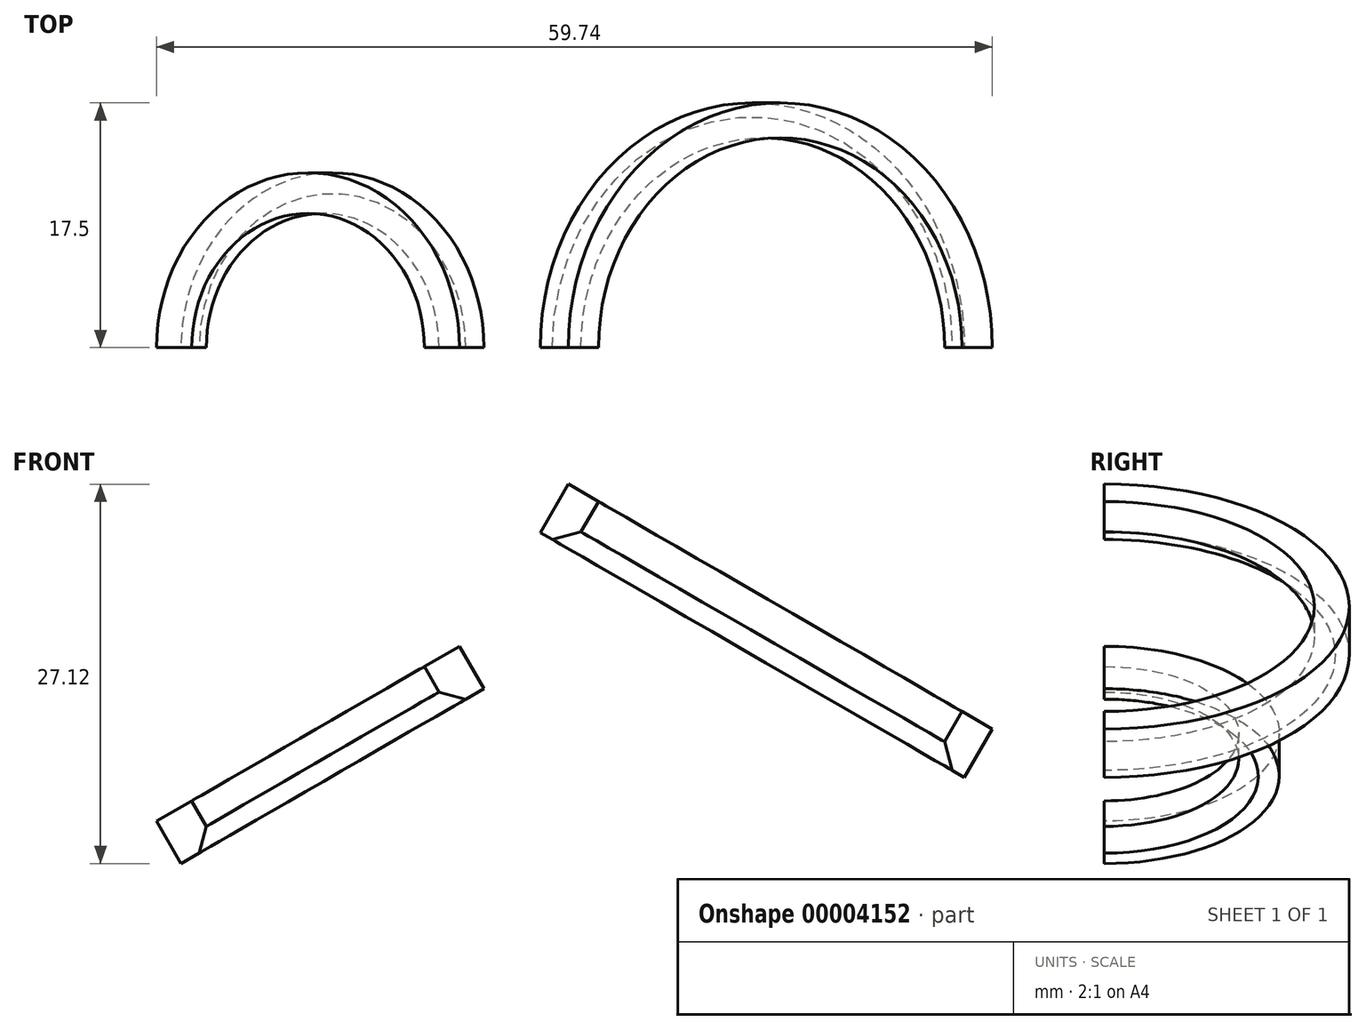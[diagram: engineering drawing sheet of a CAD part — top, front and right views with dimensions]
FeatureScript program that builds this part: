
annotation { "Feature Type Name" : "Feature", "Feature Type Description" : "" }
export const myFeature = defineFeature(function(context is Context, id is Id, definition is map)
    precondition{}
    {
        {
            var Q0;
            Q0=qCreatedBy(makeId("Top.planeOp"),FACE);
            var sketch = newSketch(context, id + "F0", { "sketchPlane" : qUnion([Q0])});
            skCircle(sketch, "E0", {"center": v(0, 0) * mm, "radius": 45 * mm});
            skSolve(sketch);
        }
        {
            var Q0;
            Q0=qCreatedBy(makeId("Front.planeOp"),FACE);
            var sketch = newSketch(context, id + "F1", { "sketchPlane" : qUnion([Q0])});
            skLineSegment(sketch, "E1", {"start": v(0, 0) * mm, "end": v(0, 101.55) * mm, "construction": true});
            skLineSegment(sketch, "E2", {"start": v(0, 0) * mm, "end": v(50.36, 87.22) * mm});
            skLineSegment(sketch, "E3.0.MirrorCS", {"start": v(0, 0) * mm, "end": v(-50.36, 87.22) * mm});
            skSolve(sketch);
        }
        {
            var Q0;
            Q0=sQuery(id+"F1.wireOp",EDGE,"E2");
            var Q1;
            Q1=sQuery(id+"F0.wireOp",VERTEX,"E0.center");
            cPlane(context, id + "F2", {"entities" : qUnion([Q0, Q1]), "cplaneType" : CPlaneType.CURVE_POINT, "offset" : 150 * mm, "width" : 150 * mm, "height" : 150 * mm});
        }
        {
            var Q0;
            Q0=qCreatedBy(id+"F2.planeOp",FACE);
            cPlane(context, id + "F3", {"entities" : qUnion([Q0]), "cplaneType" : CPlaneType.OFFSET, "offset" : 35 * mm, "width" : 150 * mm, "height" : 150 * mm});
        }
        {
            var Q0;
            Q0=qCreatedBy(id+"F3.planeOp",FACE);
            var sketch = newSketch(context, id + "F4", { "sketchPlane" : qUnion([Q0])});
            skPoint(sketch, "E4.0", {"position": v(0, 0) * mm});
            skCircle(sketch, "E5", {"center": v(0, 0) * mm, "radius": 17.5 * mm});
            skSolve(sketch);
        }
        {
            var Q0;
            Q0=sQuery(id+"F1.wireOp",EDGE,"E3.0.MirrorCS");
            var Q1;
            Q1=sQuery(id+"F1.wireOp",VERTEX,"E2.start");
            cPlane(context, id + "F5", {"entities" : qUnion([Q0, Q1]), "cplaneType" : CPlaneType.CURVE_POINT, "offset" : 150 * mm, "width" : 150 * mm, "height" : 150 * mm});
        }
        {
            var Q0;
            Q0=qCreatedBy(id+"F5.planeOp",FACE);
            cPlane(context, id + "F6", {"entities" : qUnion([Q0]), "cplaneType" : CPlaneType.OFFSET, "offset" : 25 * mm, "width" : 150 * mm, "height" : 150 * mm});
        }
        {
            var Q0;
            Q0=qCreatedBy(id+"F6.planeOp",FACE);
            var sketch = newSketch(context, id + "F7", { "sketchPlane" : qUnion([Q0])});
            skPoint(sketch, "E6.0", {"position": v(0, 0) * mm});
            skCircle(sketch, "E7", {"center": v(0, 0) * mm, "radius": 12.5 * mm});
            skSolve(sketch);
        }
        {
            var Q0;
            Q0=qCreatedBy(makeId("Front.planeOp"),FACE);
            var sketch = newSketch(context, id + "F8", { "sketchPlane" : qUnion([Q0])});
            skLineSegment(sketch, "E8.0", {"start": v(2.34, 39.06) * mm, "end": v(32.66, 21.56) * mm});
            skLineSegment(sketch, "E9", {"start": v(32.66, 21.56) * mm, "end": v(34.66, 25.02) * mm});
            skLineSegment(sketch, "E10", {"start": v(34.66, 25.02) * mm, "end": v(32.5, 26.27) * mm});
            skLineSegment(sketch, "E11", {"start": v(32.5, 26.27) * mm, "end": v(31.24, 24.1) * mm});
            skLineSegment(sketch, "E12", {"start": v(31.24, 24.1) * mm, "end": v(31.79, 22.06) * mm});
            skLineSegment(sketch, "E13", {"start": v(31.79, 22.06) * mm, "end": v(32.66, 21.56) * mm});
            skSolve(sketch);
        }
        {
            var Q0;
            Q0=makeQuery(id+"F8.imprint","IMPRINT",FACE,{"disambiguationData":[TD([[makeQuery(id+"F8.imprint","IMPRINT",EDGE,{"derivedFrom":sQuery(id+"F8.wireOp",EDGE,"E9")}),1.0]])]});
            var Q1;
            Q1=sQuery(id+"F1.wireOp",EDGE,"E2");
            revolve(context, id + "F9", {"entities" : qUnion([Q0]), "axis" : qUnion([Q1]), "revolveType" : RevolveType.ONE_DIRECTION, "angle" : 180 * degree});
        }
        {
            var Q0;
            Q0=qCreatedBy(makeId("Front.planeOp"),FACE);
            var sketch = newSketch(context, id + "F10", { "sketchPlane" : qUnion([Q0])});
            skLineSegment(sketch, "E14.0", {"start": v(-23.33, 15.4) * mm, "end": v(-1.67, 27.9) * mm});
            skLineSegment(sketch, "E15", {"start": v(-23.33, 15.4) * mm, "end": v(-25.08, 18.43) * mm});
            skLineSegment(sketch, "E16", {"start": v(-25.08, 18.43) * mm, "end": v(-22.56, 19.88) * mm});
            skLineSegment(sketch, "E17", {"start": v(-22.56, 19.88) * mm, "end": v(-21.51, 18.06) * mm});
            skLineSegment(sketch, "E18", {"start": v(-21.51, 18.06) * mm, "end": v(-22.03, 16.15) * mm});
            skLineSegment(sketch, "E19", {"start": v(-22.03, 16.15) * mm, "end": v(-23.33, 15.4) * mm});
            skSolve(sketch);
        }
        {
            var Q0;
            Q0=makeQuery(id+"F10.imprint","IMPRINT",FACE,{"disambiguationData":[TD([[makeQuery(id+"F10.imprint","IMPRINT",EDGE,{"derivedFrom":sQuery(id+"F10.wireOp",EDGE,"E15")}),-1.0]])]});
            var Q1;
            Q1=sQuery(id+"F1.wireOp",EDGE,"E3.0.MirrorCS");
            revolve(context, id + "F11", {"entities" : qUnion([Q0]), "axis" : qUnion([Q1]), "revolveType" : RevolveType.ONE_DIRECTION, "oppositeDirection" : true, "angle" : 180 * degree});
        }
    });
